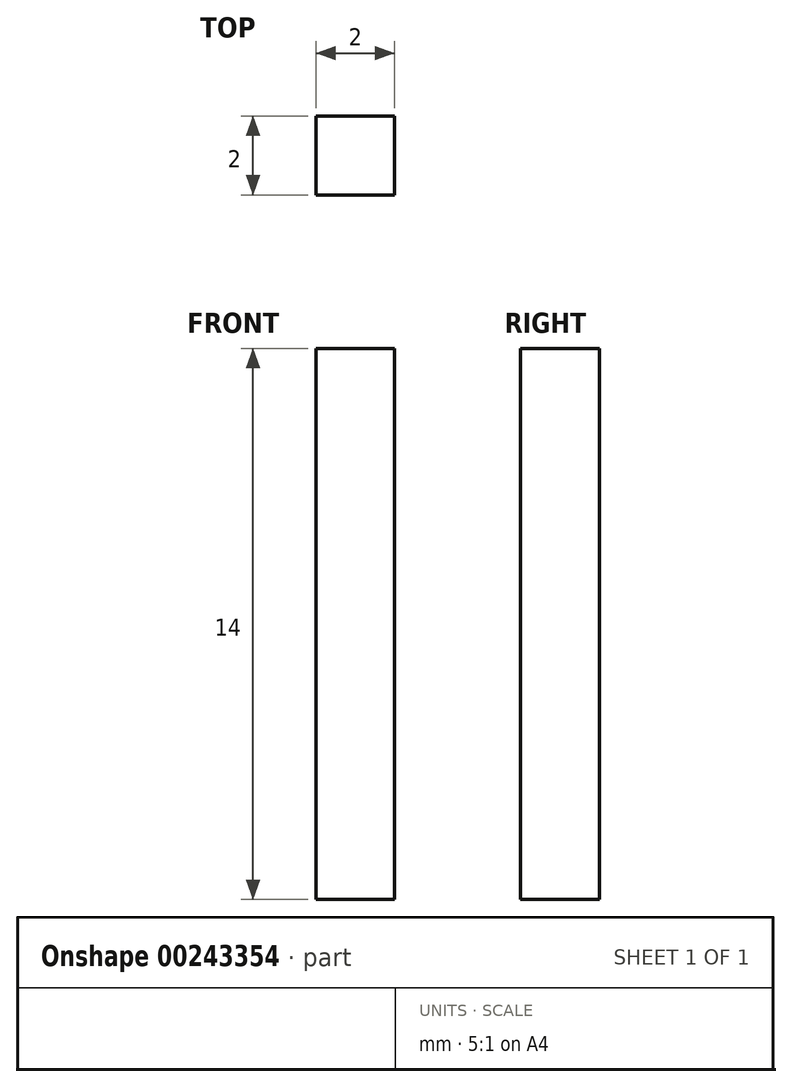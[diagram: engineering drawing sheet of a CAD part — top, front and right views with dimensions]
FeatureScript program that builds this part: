
annotation { "Feature Type Name" : "Feature", "Feature Type Description" : "" }
export const myFeature = defineFeature(function(context is Context, id is Id, definition is map)
    precondition{}
    {
        {
            var Q0;
            Q0=qCreatedBy(makeId("Top.planeOp"),FACE);
            var sketch = newSketch(context, id + "F0", { "sketchPlane" : qUnion([Q0])});
            skLineSegment(sketch, "E0.bottom", {"start": v(1, 1) * mm, "end": v(-1, 1) * mm});
            skLineSegment(sketch, "E0.top", {"start": v(1, -1) * mm, "end": v(-1, -1) * mm});
            skLineSegment(sketch, "E0.left", {"start": v(1, 1) * mm, "end": v(1, -1) * mm});
            skLineSegment(sketch, "E0.right", {"start": v(-1, 1) * mm, "end": v(-1, -1) * mm});
            skPoint(sketch, "E0.middle", {"position": v(0, 0) * mm});
            skSolve(sketch);
        }
        {
            var Q0;
            Q0 = qSketchRegion(id + "F0", true);
            extrude(context, id + "F1", {"entities" : qUnion([Q0]), "depth" : 14 * mm});
        }
    });
